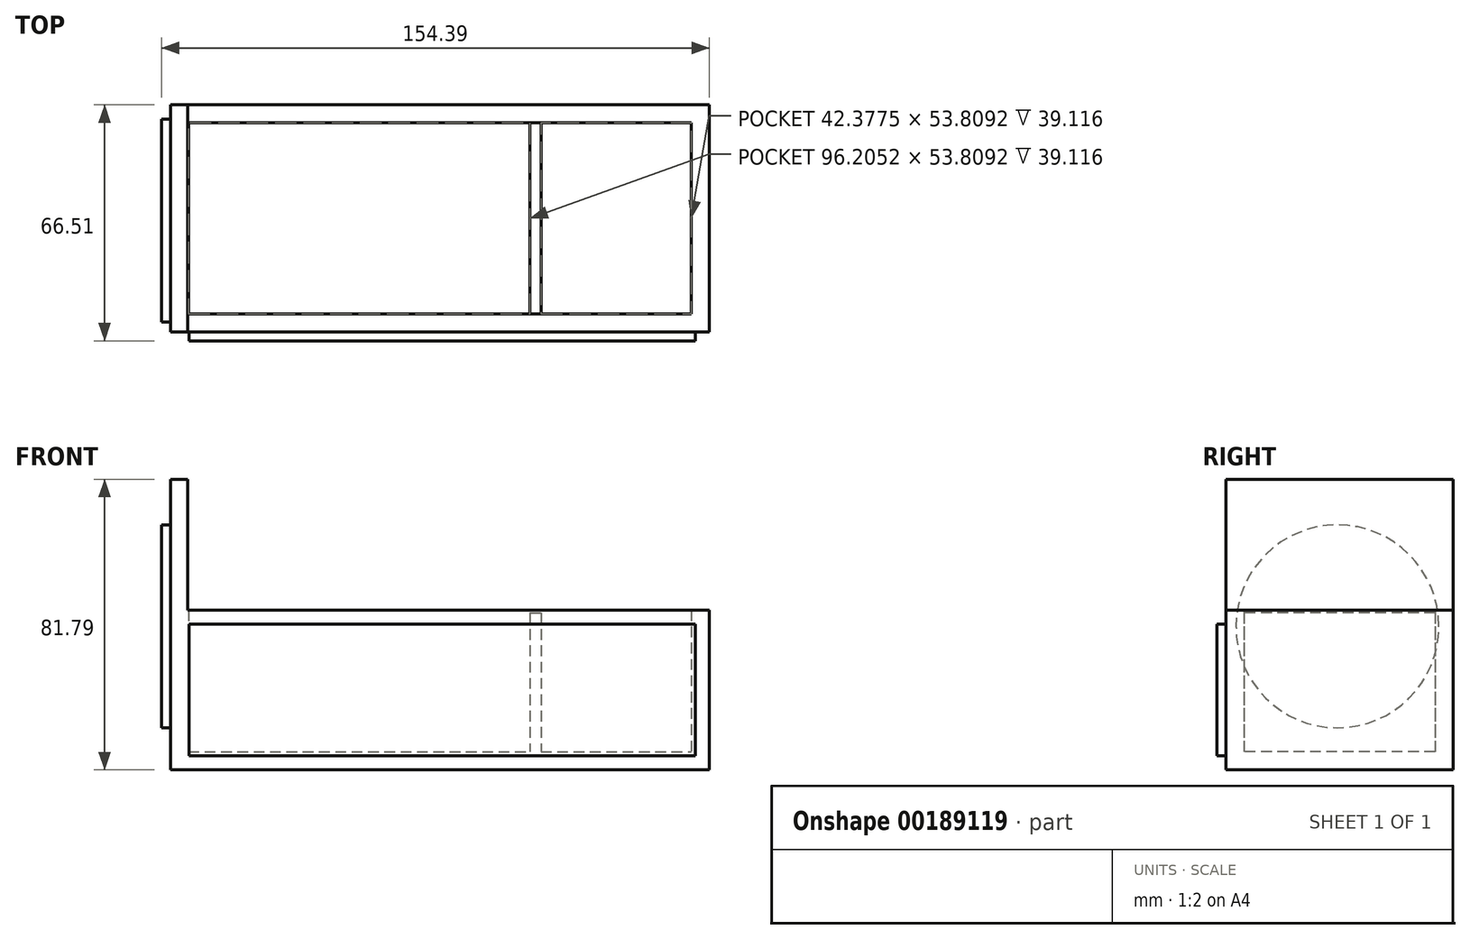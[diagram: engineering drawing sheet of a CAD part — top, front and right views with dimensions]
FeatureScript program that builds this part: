
annotation { "Feature Type Name" : "Feature", "Feature Type Description" : "" }
export const myFeature = defineFeature(function(context is Context, id is Id, definition is map)
    precondition{}
    {
        {
            var Q0;
            Q0=qCreatedBy(makeId("Top.planeOp"),FACE);
            var sketch = newSketch(context, id + "F0", { "sketchPlane" : qUnion([Q0])});
            skLineSegment(sketch, "E0.bottom", {"start": v(-76.02, 32.57) * mm, "end": v(75.83, 32.57) * mm});
            skLineSegment(sketch, "E0.top", {"start": v(-76.02, -31.4) * mm, "end": v(75.83, -31.4) * mm});
            skLineSegment(sketch, "E0.left", {"start": v(-76.02, 32.57) * mm, "end": v(-76.02, -31.4) * mm});
            skLineSegment(sketch, "E0.right", {"start": v(75.83, 32.57) * mm, "end": v(75.83, -31.4) * mm});
            skSolve(sketch);
        }
        {
            var Q0;
            Q0=makeQuery(id+"F0.imprint","IMPRINT",FACE,{"disambiguationData":[TD([[makeQuery(id+"F0.imprint","IMPRINT",EDGE,{"derivedFrom":sQuery(id+"F0.wireOp",EDGE,"E0.bottom")}),-1.0]])]});
            extrude(context, id + "F1", {"entities" : qUnion([Q0]), "depth" : 44.96 * mm});
        }
        {
            var Q0;
            Q0=makeQuery(id+"F1.opExtrude","CAP_FACE",FACE,{"disambiguationData":[OSD([sQuery(id+"F0.wireOp",EDGE,"E0.bottom"),sQuery(id+"F0.wireOp",EDGE,"E0.top"),sQuery(id+"F0.wireOp",EDGE,"E0.left"),sQuery(id+"F0.wireOp",EDGE,"E0.right")])],"isStart":false});
            shell(context, id + "F2", {"entities" : qUnion([Q0]), "thickness" : 5.08 * mm});
        }
        {
            var Q0;
            Q0=makeQuery(id+"F1.opExtrude","CAP_FACE",FACE,{"disambiguationData":[OSD([sQuery(id+"F0.wireOp",EDGE,"E0.bottom"),sQuery(id+"F0.wireOp",EDGE,"E0.top"),sQuery(id+"F0.wireOp",EDGE,"E0.left"),sQuery(id+"F0.wireOp",EDGE,"E0.right")])],"isStart":false});
            var sketch = newSketch(context, id + "F3", { "sketchPlane" : qUnion([Q0])});
            skLineSegment(sketch, "E1.bottom", {"start": v(-76.02, 32.57) * mm, "end": v(-71.16, 32.57) * mm});
            skLineSegment(sketch, "E1.top", {"start": v(-76.02, -31.4) * mm, "end": v(-71.16, -31.4) * mm});
            skLineSegment(sketch, "E1.left", {"start": v(-76.02, 32.57) * mm, "end": v(-76.02, -31.4) * mm});
            skLineSegment(sketch, "E1.right", {"start": v(-71.16, 32.57) * mm, "end": v(-71.16, -31.4) * mm});
            skSolve(sketch);
        }
        {
            var Q0;
            Q0=makeQuery(id+"F3.imprint","IMPRINT",FACE,{"disambiguationData":[TD([[makeQuery(id+"F3.imprint","IMPRINT",EDGE,{"derivedFrom":sQuery(id+"F3.wireOp",EDGE,"E1.bottom")}),-1.0]])]});
            extrude(context, id + "F4", {"entities" : qUnion([Q0]), "operationType" : NewBodyOperationType.ADD, "depth" : 36.83 * mm});
        }
        {
            var Q0;
            Q0=makeQuery(id+"F4.boolean.opBoolean","MERGE",FACE,{"derivedFrom":[makeQuery(id+"F1.opExtrude","SWEPT_FACE",FACE,{"disambiguationData":[OSD([sQuery(id+"F0.wireOp",EDGE,"E0.left")])]}),makeQuery(id+"F4.opExtrude","SWEPT_FACE",FACE,{"disambiguationData":[OSD([sQuery(id+"F3.wireOp",EDGE,"E1.left")])]})]});
            var sketch = newSketch(context, id + "F5", { "sketchPlane" : qUnion([Q0])});
            skCircle(sketch, "E2", {"center": v(0, 40.4) * mm, "radius": 28.58 * mm});
            skSolve(sketch);
        }
        {
            var Q0;
            Q0 = qSketchRegion(id + "F5", true);
            extrude(context, id + "F6", {"entities" : qUnion([Q0]), "operationType" : NewBodyOperationType.ADD, "depth" : 2.54 * mm});
        }
        {
            var Q0;
            Q0=makeQuery(id+"F4.boolean.opBoolean","MERGE",FACE,{"derivedFrom":[makeQuery(id+"F1.opExtrude","SWEPT_FACE",FACE,{"disambiguationData":[OSD([sQuery(id+"F0.wireOp",EDGE,"E0.top")])]}),makeQuery(id+"F4.opExtrude","SWEPT_FACE",FACE,{"disambiguationData":[OSD([sQuery(id+"F3.wireOp",EDGE,"E1.top")])]})]});
            var sketch = newSketch(context, id + "F7", { "sketchPlane" : qUnion([Q0])});
            skLineSegment(sketch, "E3.bottom", {"start": v(-70.72, 41) * mm, "end": v(71.78, 41) * mm});
            skLineSegment(sketch, "E3.top", {"start": v(-70.72, 3.9) * mm, "end": v(71.78, 3.9) * mm});
            skLineSegment(sketch, "E3.left", {"start": v(-70.72, 41) * mm, "end": v(-70.72, 3.9) * mm});
            skLineSegment(sketch, "E3.right", {"start": v(71.78, 41) * mm, "end": v(71.78, 3.9) * mm});
            skSolve(sketch);
        }
        {
            var Q0;
            Q0=makeQuery(id+"F7.imprint","IMPRINT",FACE,{"disambiguationData":[TD([[makeQuery(id+"F7.imprint","IMPRINT",EDGE,{"derivedFrom":sQuery(id+"F7.wireOp",EDGE,"E3.bottom")}),-1.0]])]});
            extrude(context, id + "F8", {"entities" : qUnion([Q0]), "operationType" : NewBodyOperationType.ADD, "depth" : 2.54 * mm});
        }
        {
            var Q0;
            Q0=makeQuery(id+"F2.opShell","OFFSET_FACE",FACE,{"disambiguationData":[OSD([sQuery(id+"F0.wireOp",EDGE,"E0.bottom"),sQuery(id+"F0.wireOp",EDGE,"E0.top"),sQuery(id+"F0.wireOp",EDGE,"E0.left"),sQuery(id+"F0.wireOp",EDGE,"E0.right")])]});
            var sketch = newSketch(context, id + "F9", { "sketchPlane" : qUnion([Q0])});
            skLineSegment(sketch, "E4.bottom", {"start": v(25.26, 27.49) * mm, "end": v(28.37, 27.49) * mm});
            skLineSegment(sketch, "E4.top", {"start": v(25.26, -26.32) * mm, "end": v(28.37, -26.32) * mm});
            skLineSegment(sketch, "E4.left", {"start": v(25.26, 27.49) * mm, "end": v(25.26, -26.32) * mm});
            skLineSegment(sketch, "E4.right", {"start": v(28.37, 27.49) * mm, "end": v(28.37, -26.32) * mm});
            skSolve(sketch);
        }
        {
            var Q0;
            Q0 = qSketchRegion(id + "F9", true);
            extrude(context, id + "F10", {"entities" : qUnion([Q0]), "operationType" : NewBodyOperationType.ADD, "depth" : 39.12 * mm});
        }
    });
